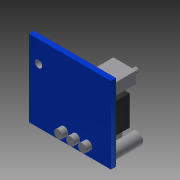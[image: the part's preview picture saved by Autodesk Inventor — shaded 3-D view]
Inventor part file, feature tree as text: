
AUTODESK INVENTOR PART (.ipt)
format: ipt  version: 2015 (Build 190159000, 159)  size: 511,488 bytes
history: native  units: mm
features: extrude x10, sketch x2, chamfer x1
ambient origin geometry x8: Origin, YZ Plane, XZ Plane, XY Plane, X Axis, Y Axis, Z Axis, Center Point
bodies: Solid1 (feature_tree)
feature tree (13):
  sketch  "Sketch1"  dims[d0=34.28mm d1=32.0mm]
  extrude  "Extrusion1"  Depth=32.0mm
  extrude  "Extrusion2"  Depth=4.05mm
  extrude  "Extrusion3"  Depth=8.95mm
  chamfer  "Chamfer1"  Distance=10.13mm
  extrude  "Extrusion4"  Depth=6.0mm
  extrude  "Extrusion5"  Depth=6.0mm
  extrude  "Extrusion6"  Depth=3.5mm
  extrude  "Extrusion7"  Depth=3.5mm
  extrude  "Extrusion8"  Depth=3.5mm
  extrude  "Extrusion9"  Depth=5.0mm
  extrude  "Extrusion10"  Depth=5.0mm
  sketch  "Sketch2"  dims[d2=3.0mm d3=4.05mm d4=8.95mm d5=10.13mm d6=6.0mm d7=6.0mm d8=3.5mm d9=3.5mm d10=3.5mm d11=5.0mm d12=5.0mm d13=5.0mm d14=3.0mm d15=3.0mm d16=12.5mm d17=12.5mm d18=15.0mm d19=7.5mm d20=2.0mm d21=9.53mm d22=4.82mm d23=1.330787mm d24=1.331mm d25=2.15mm d26=0.0mm d27=19.17mm d28=0.0mm d29=11.77mm d30=0.0mm d31=1.5mm d32=2.0mm d33=45.0deg d34=10.0mm d35=0.0mm d36=13.91mm d37=0.0mm d38=9.14mm d39=0.0mm d40=11.85mm d41=0.0mm d42=2.31mm d43=1.5mm d44=1.5mm d45=13.61mm d46=0.0mm d47=2.4mm d48=0.0mm d49=1.0mm d50=0.0mm]
